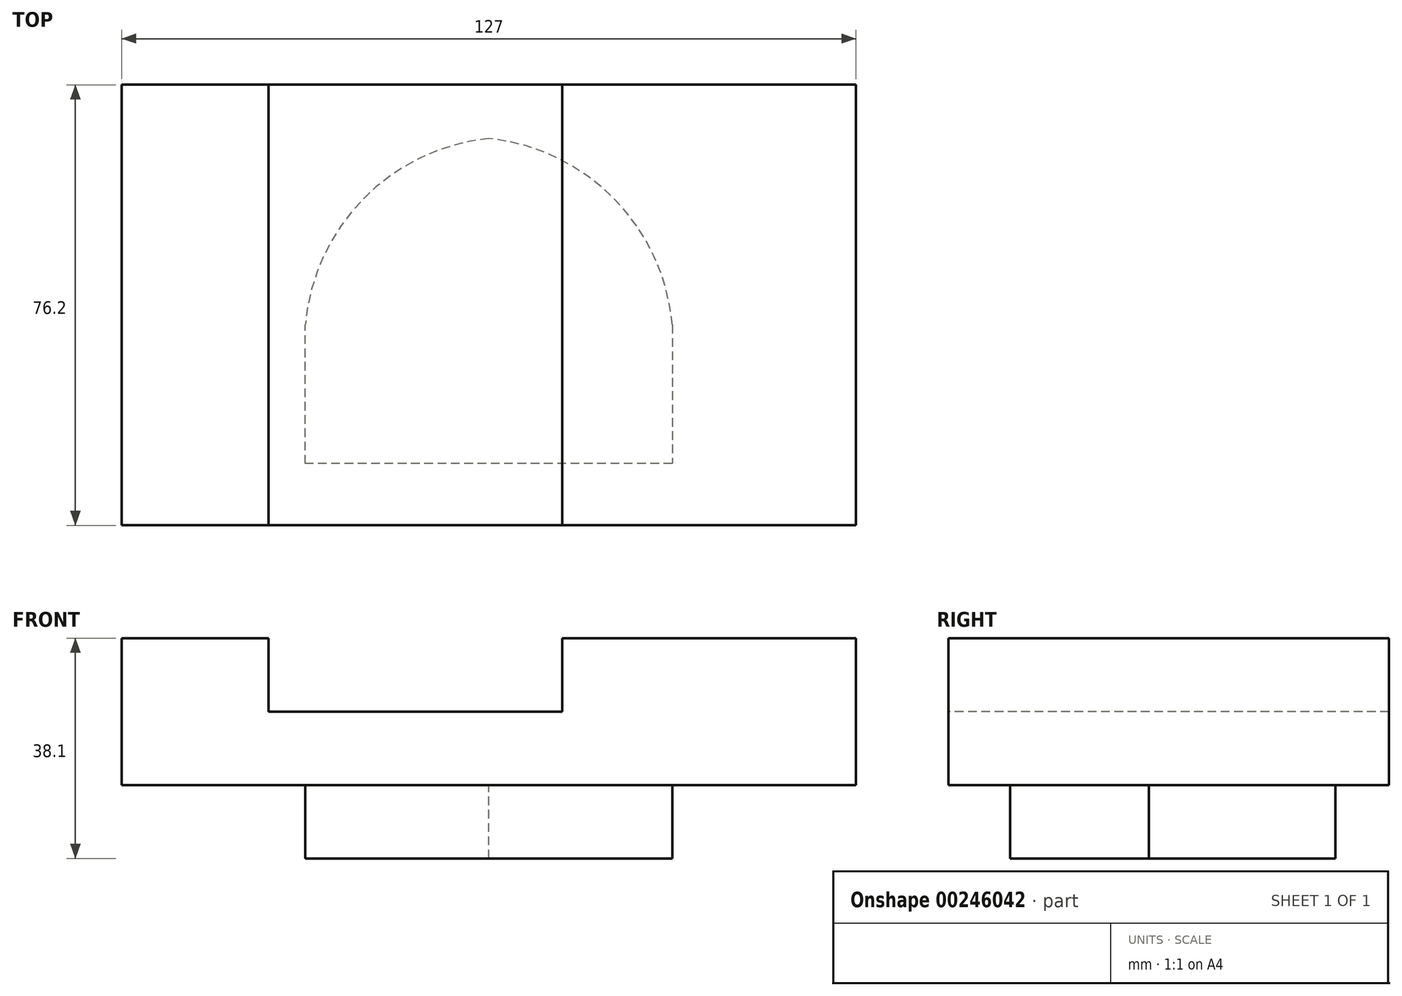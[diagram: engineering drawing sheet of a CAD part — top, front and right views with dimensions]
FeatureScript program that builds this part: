
annotation { "Feature Type Name" : "Feature", "Feature Type Description" : "" }
export const myFeature = defineFeature(function(context is Context, id is Id, definition is map)
    precondition{}
    {
        {
            var Q0;
            Q0=qCreatedBy(makeId("Top.planeOp"),FACE);
            var sketch = newSketch(context, id + "F0", { "sketchPlane" : qUnion([Q0])});
            skLineSegment(sketch, "E0", {"start": v(-68.24, 47.78) * mm, "end": v(-68.24, -28.42) * mm});
            skLineSegment(sketch, "E1", {"start": v(-68.24, 47.78) * mm, "end": v(-42.84, 47.78) * mm});
            skLineSegment(sketch, "E2", {"start": v(-68.24, -28.42) * mm, "end": v(-42.84, -28.42) * mm});
            skLineSegment(sketch, "E3", {"start": v(7.96, 47.78) * mm, "end": v(58.76, 47.78) * mm});
            skLineSegment(sketch, "E4", {"start": v(58.76, 47.78) * mm, "end": v(58.76, -28.42) * mm});
            skLineSegment(sketch, "E5", {"start": v(7.96, -28.42) * mm, "end": v(58.76, -28.42) * mm});
            skLineSegment(sketch, "E6", {"start": v(-42.84, 47.78) * mm, "end": v(7.96, 47.78) * mm});
            skLineSegment(sketch, "E7", {"start": v(-42.84, -28.42) * mm, "end": v(7.96, -28.42) * mm});
            skSolve(sketch);
        }
        {
            var Q0;
            Q0=makeQuery(id+"F0.imprint","IMPRINT",FACE,{"disambiguationData":[TD([[makeQuery(id+"F0.imprint","IMPRINT",EDGE,{"derivedFrom":sQuery(id+"F0.wireOp",EDGE,"E0")}),1.0]])]});
            extrude(context, id + "F1", {"entities" : qUnion([Q0]), "depth" : 12.7 * mm});
        }
        {
            var Q0;
            Q0=makeQuery(id+"F1.opExtrude","CAP_FACE",FACE,{"disambiguationData":[OSD([sQuery(id+"F0.wireOp",EDGE,"E0"),sQuery(id+"F0.wireOp",EDGE,"E1"),sQuery(id+"F0.wireOp",EDGE,"E2"),sQuery(id+"F0.wireOp",EDGE,"E3"),sQuery(id+"F0.wireOp",EDGE,"E4"),sQuery(id+"F0.wireOp",EDGE,"E5"),sQuery(id+"F0.wireOp",EDGE,"E6"),sQuery(id+"F0.wireOp",EDGE,"E7")])],"isStart":false});
            var sketch = newSketch(context, id + "F2", { "sketchPlane" : qUnion([Q0])});
            skLineSegment(sketch, "E8", {"start": v(-42.84, 47.78) * mm, "end": v(-42.84, -28.42) * mm});
            skLineSegment(sketch, "E9", {"start": v(7.96, 47.78) * mm, "end": v(7.96, -28.42) * mm});
            skSolve(sketch);
        }
        {
            var Q0;
            {var subQ0=sQuery(id+"F2.wireOp",EDGE,"E8");Q0=makeQuery(id+"F2.imprint","IMPRINT",FACE,{"disambiguationData":[TD([[makeQuery(id+"F2.imprint","IMPRINT",EDGE,{"derivedFrom":subQ0}),-1.0]])]});}
            extrude(context, id + "F3", {"entities" : qUnion([Q0]), "operationType" : NewBodyOperationType.ADD, "depth" : 12.7 * mm});
        }
        {
            var Q0;
            Q0=makeQuery(id+"F1.opExtrude","CAP_FACE",FACE,{"disambiguationData":[OSD([sQuery(id+"F0.wireOp",EDGE,"E0"),sQuery(id+"F0.wireOp",EDGE,"E1"),sQuery(id+"F0.wireOp",EDGE,"E2"),sQuery(id+"F0.wireOp",EDGE,"E3"),sQuery(id+"F0.wireOp",EDGE,"E4"),sQuery(id+"F0.wireOp",EDGE,"E5"),sQuery(id+"F0.wireOp",EDGE,"E6"),sQuery(id+"F0.wireOp",EDGE,"E7")])],"isStart":false});
            var sketch = newSketch(context, id + "F4", { "sketchPlane" : qUnion([Q0])});
            skLineSegment(sketch, "E10", {"start": v(7.96, 47.78) * mm, "end": v(7.96, -28.42) * mm});
            skSolve(sketch);
        }
        {
            var Q0;
            {var subQ0=sQuery(id+"F4.wireOp",EDGE,"E10");Q0=makeQuery(id+"F4.imprint","IMPRINT",FACE,{"disambiguationData":[TD([[makeQuery(id+"F4.imprint","IMPRINT",EDGE,{"derivedFrom":subQ0}),1.0]])]});}
            extrude(context, id + "F5", {"entities" : qUnion([Q0]), "operationType" : NewBodyOperationType.ADD, "depth" : 12.7 * mm});
        }
        {
            var Q0;
            Q0=makeQuery(id+"F1.opExtrude","CAP_FACE",FACE,{"disambiguationData":[OSD([sQuery(id+"F0.wireOp",EDGE,"E0"),sQuery(id+"F0.wireOp",EDGE,"E1"),sQuery(id+"F0.wireOp",EDGE,"E2"),sQuery(id+"F0.wireOp",EDGE,"E3"),sQuery(id+"F0.wireOp",EDGE,"E4"),sQuery(id+"F0.wireOp",EDGE,"E5"),sQuery(id+"F0.wireOp",EDGE,"E6"),sQuery(id+"F0.wireOp",EDGE,"E7")])],"isStart":true});
            var sketch = newSketch(context, id + "F6", { "sketchPlane" : qUnion([Q0])});
            skPoint(sketch, "E11.start.orphan", {"position": v(-4.74, 28.42) * mm});
            skLineSegment(sketch, "E12", {"start": v(-4.74, 17.75) * mm, "end": v(-36.49, 17.75) * mm});
            skLineSegment(sketch, "E13", {"start": v(-4.74, 17.75) * mm, "end": v(27.01, 17.75) * mm});
            skLineSegment(sketch, "E14", {"start": v(-36.49, 17.75) * mm, "end": v(-36.49, -6.26) * mm});
            skLineSegment(sketch, "E15", {"start": v(27.01, -6.26) * mm, "end": v(27.01, 17.75) * mm});
            skArc(sketch, "E16", {"start": v(-36.49, 0) * mm, "mid": v(-28.5, -25.76) * mm, "end": v(-4.74, -38.5) * mm});
            skArc(sketch, "E17", {"start": v(-4.74, -38.5) * mm, "mid": v(19.02, -25.76) * mm, "end": v(27.01, 0) * mm});
            skPoint(sketch, "E18.orphan", {"position": v(-36.49, -38.5) * mm});
            skPoint(sketch, "E19.orphan", {"position": v(27.01, -38.5) * mm});
            skSolve(sketch);
        }
        {
            var Q0;
            {var subQ4=sQuery(id+"F6.wireOp",EDGE,"E12");Q0=makeQuery(id+"F6.imprint","IMPRINT",FACE,{"disambiguationData":[TD([[makeQuery(id+"F6.imprint","IMPRINT",EDGE,{"derivedFrom":subQ4}),1.0]])]});}
            extrude(context, id + "F7", {"entities" : qUnion([Q0]), "operationType" : NewBodyOperationType.ADD, "depth" : 12.7 * mm});
        }
    });
